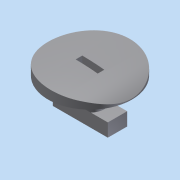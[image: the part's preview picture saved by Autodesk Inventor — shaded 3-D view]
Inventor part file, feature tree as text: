
AUTODESK INVENTOR PART (.ipt)
format: ipt  version: 2011 SP2 (Build 150309200, 309)  size: 150,016 bytes
history: native  units: mm
features: projected_geometry x6, sketch x5, extrude x4, revolve x1
ambient origin geometry x8: Origin, YZ Plane, XZ Plane, XY Plane, X Axis, Y Axis, Z Axis, Center Point
bodies: Solid1 (feature_tree)
feature tree (16):
  extrude  "Extrusion1"  Depth=1.5mm
  extrude  "Extrusion2"  Depth=2.3mm TaperAngle=0.0deg
  revolve  "Revolution1"  [1 undecoded]
  extrude  "Extrusion3"  Depth=4.0mm
  extrude  "Extrusion4"  Depth=3.25mm
  sketch  "Sketch1"  dims[d0=19.0mm d1=1.5mm]
  sketch  "Sketch2"  dims[d2=5.0mm d3=2.3mm d4=0.0mm]
  projected_geometry  "Projected Loop1"
  projected_geometry  "Projected Loop2"
  sketch  "Sketch3"  dims[d5=12.0mm d6=0.2mm]
  projected_geometry  "Projected Loop3"
  sketch  "Sketch4"  dims[d8=1.9mm d9=4.0mm]
  projected_geometry  "Projected Loop4"
  sketch  "Sketch5"  dims[d10=10.0mm d11=0.0mm d12=3.25mm d13=5.0mm d14=90.0deg d16=3.0mm d17=12.5mm d19=2.2mm d20=2.2mm d21=0.0mm d22=0.0mm d23=1.0mm d24=2.2mm d25=0.0mm]
  projected_geometry  "Projected Loop5"
  projected_geometry  "Projected Loop6"
note: 1 required parameter value undecoded (feature->parameter linkage not recoverable at this tier; creation-order binding heuristic only, values carry confidence <= 0.55)
